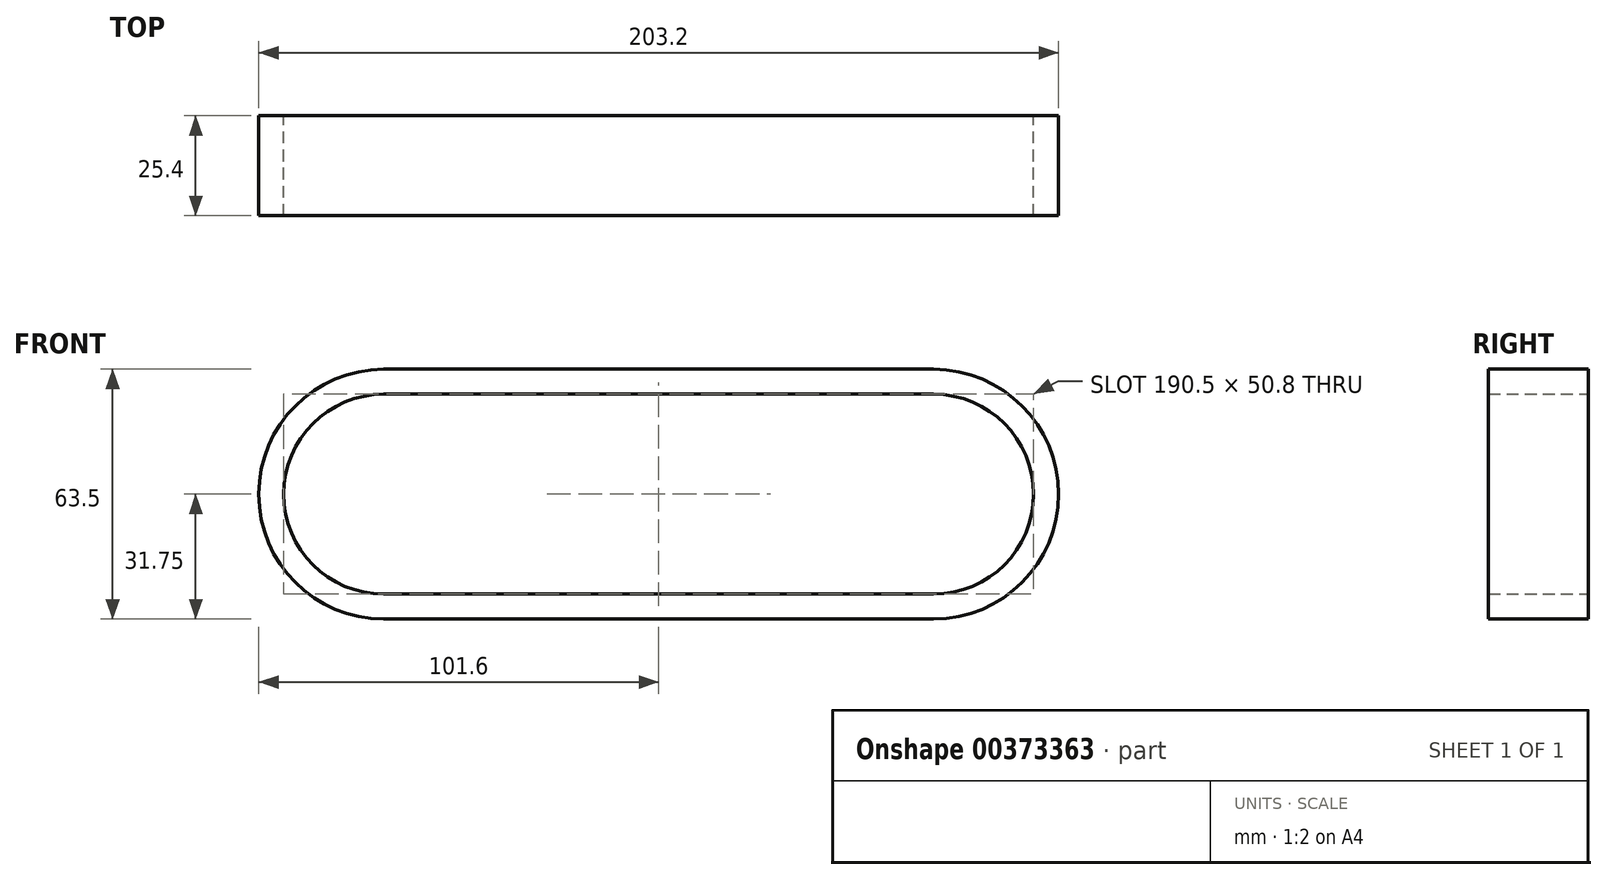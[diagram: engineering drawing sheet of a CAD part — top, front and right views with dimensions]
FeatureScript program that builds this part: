
annotation { "Feature Type Name" : "Feature", "Feature Type Description" : "" }
export const myFeature = defineFeature(function(context is Context, id is Id, definition is map)
    precondition{}
    {
        {
            var Q0;
            Q0=qCreatedBy(makeId("Front.planeOp"),FACE);
            var sketch = newSketch(context, id + "F0", { "sketchPlane" : qUnion([Q0])});
            skLineSegment(sketch, "E0.bottom", {"start": v(69.85, 25.4) * mm, "end": v(-69.85, 25.4) * mm});
            skLineSegment(sketch, "E0.top", {"start": v(69.85, -25.4) * mm, "end": v(-69.85, -25.4) * mm});
            skLineSegment(sketch, "E0.left", {"start": v(95.25, 0) * mm, "end": v(95.25, 0) * mm});
            skLineSegment(sketch, "E0.right", {"start": v(-95.25, 0) * mm, "end": v(-95.25, 0) * mm});
            skPoint(sketch, "E0.middle", {"position": v(0, 0) * mm});
            skPoint(sketch, "E1.visualSharp", {"position": v(-95.25, 25.4) * mm});
            skArc(sketch, "E1.filletArc", {"start": v(-69.85, 25.4) * mm, "mid": v(-87.81, 17.96) * mm, "end": v(-95.25, 0) * mm});
            skPoint(sketch, "E2.visualSharp", {"position": v(-95.25, -25.4) * mm});
            skArc(sketch, "E2.filletArc", {"start": v(-95.25, 0) * mm, "mid": v(-87.81, -17.96) * mm, "end": v(-69.85, -25.4) * mm});
            skPoint(sketch, "E3.visualSharp", {"position": v(95.25, -25.4) * mm});
            skArc(sketch, "E3.filletArc", {"start": v(69.85, -25.4) * mm, "mid": v(87.81, -17.96) * mm, "end": v(95.25, 0) * mm});
            skPoint(sketch, "E4.visualSharp", {"position": v(95.25, 25.4) * mm});
            skArc(sketch, "E4.filletArc", {"start": v(95.25, 0) * mm, "mid": v(87.81, 17.96) * mm, "end": v(69.85, 25.4) * mm});
            skLineSegment(sketch, "E5.bottom", {"start": v(-69.85, 31.75) * mm, "end": v(69.85, 31.75) * mm});
            skLineSegment(sketch, "E5.top", {"start": v(-69.85, -31.75) * mm, "end": v(69.85, -31.75) * mm});
            skLineSegment(sketch, "E5.left", {"start": v(-101.6, 0) * mm, "end": v(-101.6, 0) * mm});
            skLineSegment(sketch, "E5.right", {"start": v(101.6, 0) * mm, "end": v(101.6, 0) * mm});
            skPoint(sketch, "E6.visualSharp", {"position": v(-101.6, 31.75) * mm});
            skArc(sketch, "E6.filletArc", {"start": v(-69.85, 31.75) * mm, "mid": v(-92.3, 22.45) * mm, "end": v(-101.6, 0) * mm});
            skPoint(sketch, "E7.visualSharp", {"position": v(-101.6, -31.75) * mm});
            skArc(sketch, "E7.filletArc", {"start": v(-101.6, 0) * mm, "mid": v(-92.3, -22.45) * mm, "end": v(-69.85, -31.75) * mm});
            skPoint(sketch, "E8.visualSharp", {"position": v(101.6, -31.75) * mm});
            skArc(sketch, "E8.filletArc", {"start": v(69.85, -31.75) * mm, "mid": v(92.3, -22.45) * mm, "end": v(101.6, 0) * mm});
            skPoint(sketch, "E9.visualSharp", {"position": v(101.6, 31.75) * mm});
            skArc(sketch, "E9.filletArc", {"start": v(101.6, 0) * mm, "mid": v(92.3, 22.45) * mm, "end": v(69.85, 31.75) * mm});
            skSolve(sketch);
        }
        {
            var Q0;
            Q0=makeQuery(id+"F0.imprint","IMPRINT",FACE,{"disambiguationData":[TD([[makeQuery(id+"F0.imprint","IMPRINT",EDGE,{"derivedFrom":sQuery(id+"F0.wireOp",EDGE,"E0.bottom")}),-1.0]])]});
            extrude(context, id + "F1", {"entities" : qUnion([Q0]), "depth" : 25.4 * mm});
        }
    });
